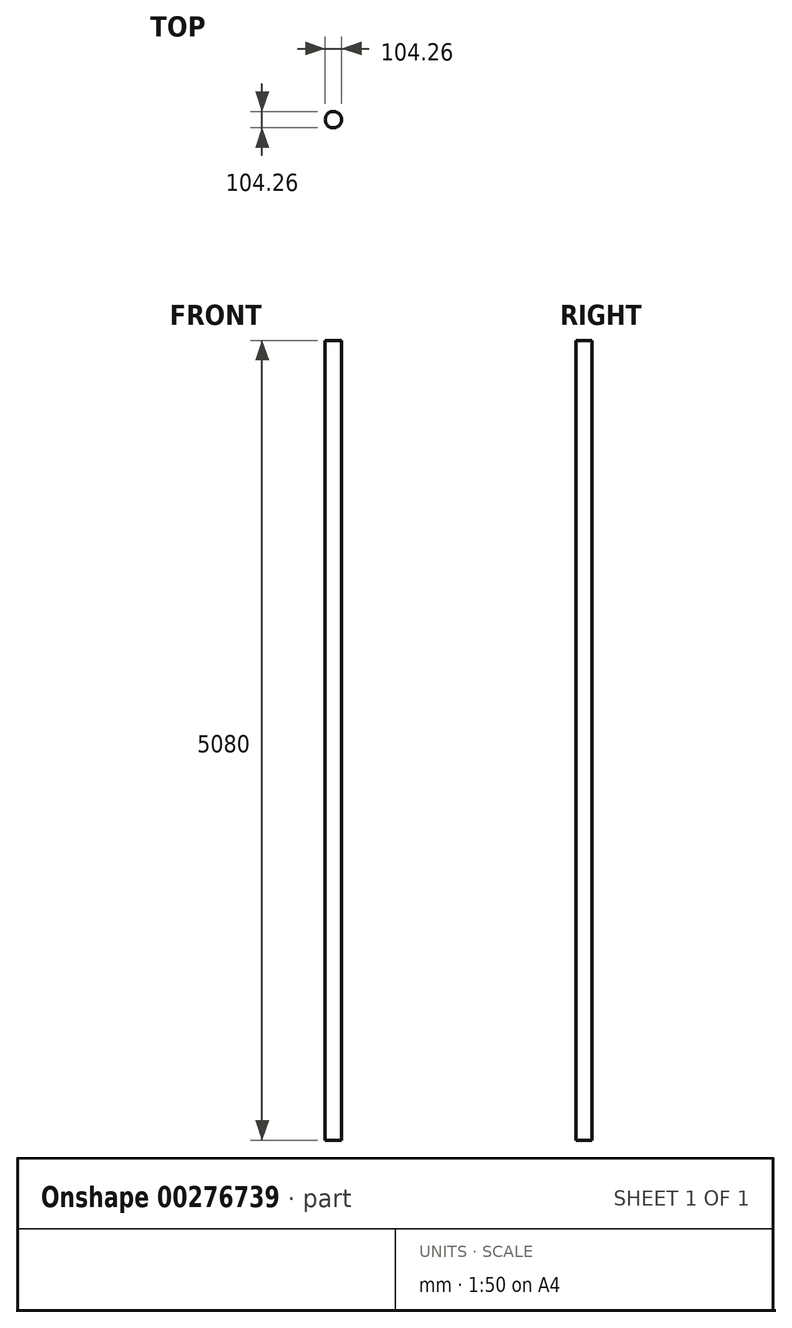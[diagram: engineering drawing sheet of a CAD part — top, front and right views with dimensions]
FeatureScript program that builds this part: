
annotation { "Feature Type Name" : "Feature", "Feature Type Description" : "" }
export const myFeature = defineFeature(function(context is Context, id is Id, definition is map)
    precondition{}
    {
        {
            var Q0;
            Q0=qCreatedBy(makeId("Top.planeOp"),FACE);
            var sketch = newSketch(context, id + "F0", { "sketchPlane" : qUnion([Q0])});
            skCircle(sketch, "E0", {"center": v(0, 0) * mm, "radius": 52.13 * mm});
            skSolve(sketch);
        }
        {
            var Q0;
            Q0=sQuery(id+"F0.wireOp",EDGE,"E0");
            extrude(context, id + "F1", {"bodyType" : ToolBodyType.SURFACE, "surfaceEntities" : qUnion([Q0]), "depth" : 5080 * mm});
        }
    });
